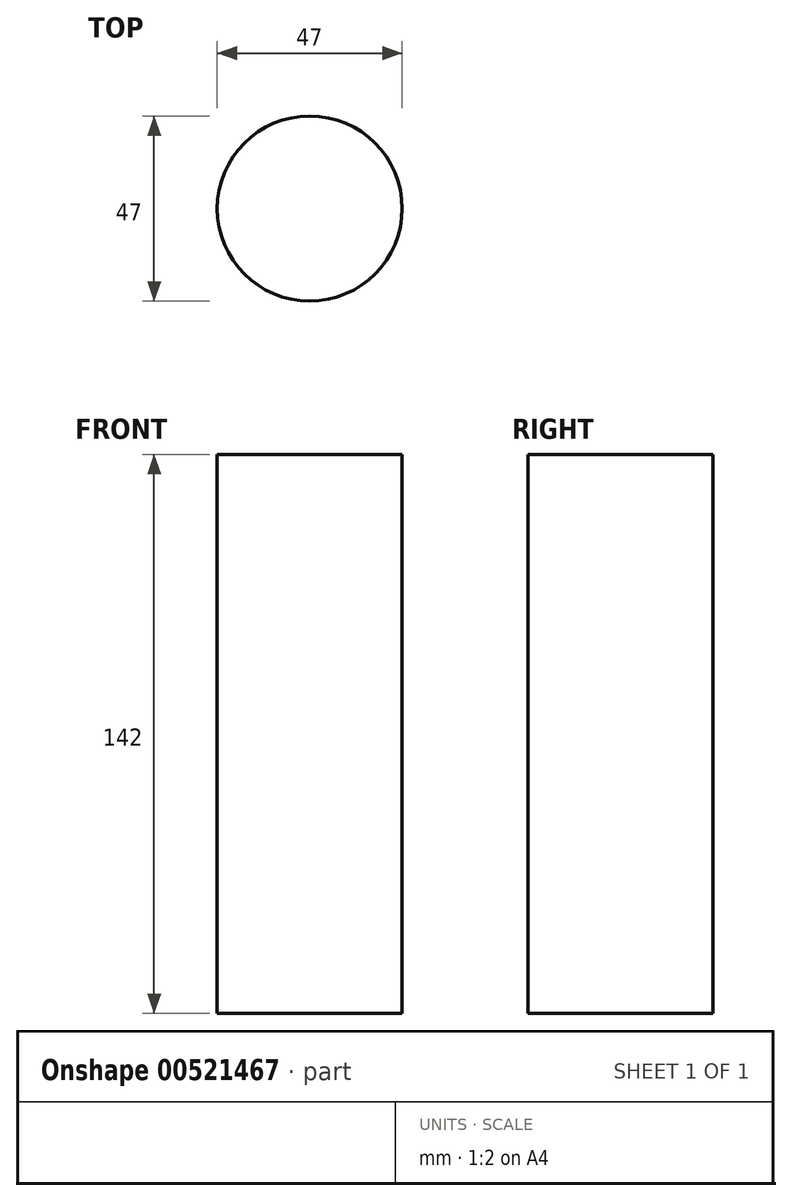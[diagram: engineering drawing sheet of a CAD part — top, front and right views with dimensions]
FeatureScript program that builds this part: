
annotation { "Feature Type Name" : "Feature", "Feature Type Description" : "" }
export const myFeature = defineFeature(function(context is Context, id is Id, definition is map)
    precondition{}
    {
        {
            var Q0;
            Q0=qCreatedBy(makeId("Top.planeOp"),FACE);
            var sketch = newSketch(context, id + "F0", { "sketchPlane" : qUnion([Q0])});
            skCircle(sketch, "E0", {"center": v(0, 0) * mm, "radius": 23.5 * mm});
            skSolve(sketch);
        }
        {
            var Q0;
            Q0 = qSketchRegion(id + "F0", true);
            extrude(context, id + "F1", {"entities" : qUnion([Q0]), "depth" : 142 * mm, "offsetDistance" : 25.4 * mm});
        }
    });
